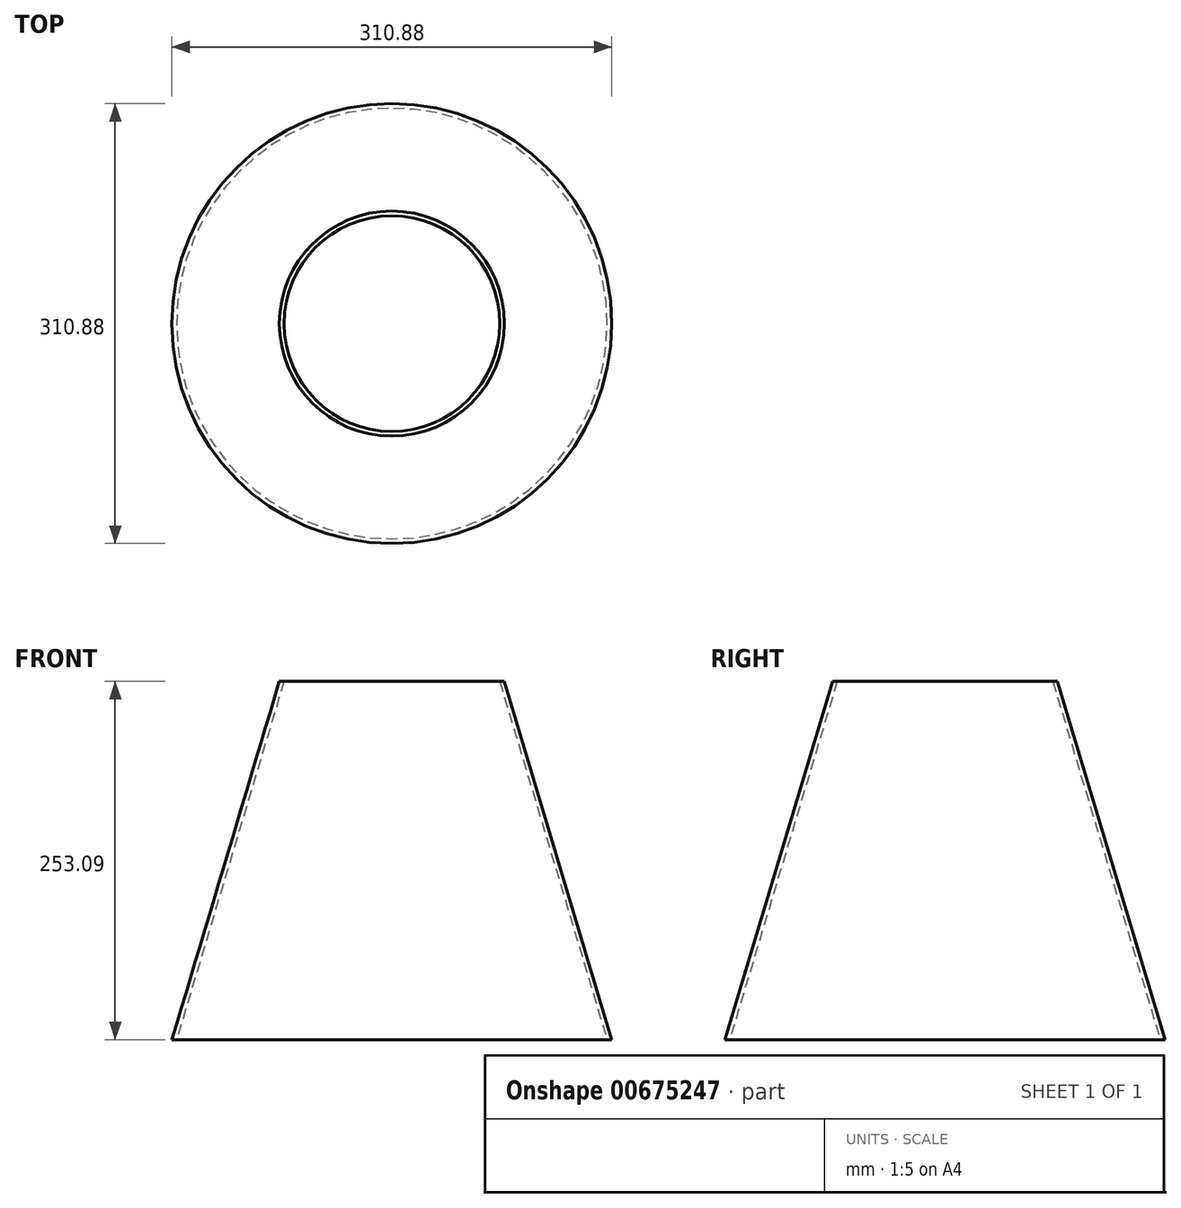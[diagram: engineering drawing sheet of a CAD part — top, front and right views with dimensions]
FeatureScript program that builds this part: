
annotation { "Feature Type Name" : "Feature", "Feature Type Description" : "" }
export const myFeature = defineFeature(function(context is Context, id is Id, definition is map)
    precondition{}
    {
        {
            var Q0;
            Q0=qCreatedBy(makeId("Front.planeOp"),FACE);
            var sketch = newSketch(context, id + "F0", { "sketchPlane" : qUnion([Q0])});
            skLineSegment(sketch, "E0", {"start": v(0, 0) * mm, "end": v(152.4, 0) * mm, "construction": true});
            skLineSegment(sketch, "E1", {"start": v(0, 0) * mm, "end": v(0, 254) * mm, "construction": true});
            skLineSegment(sketch, "E2", {"start": v(0, 254) * mm, "end": v(76.2, 254) * mm, "construction": true});
            skLineSegment(sketch, "E3", {"start": v(152.4, 0) * mm, "end": v(76.2, 254) * mm, "construction": true});
            skLineSegment(sketch, "E4.0", {"start": v(155.44, 0.91) * mm, "end": v(79.51, 254) * mm});
            skLineSegment(sketch, "E5", {"start": v(76.2, 254) * mm, "end": v(79.51, 254) * mm});
            skLineSegment(sketch, "E6", {"start": v(155.44, 0.91) * mm, "end": v(152.13, 0.91) * mm});
            skLineSegment(sketch, "E7", {"start": v(76.2, 254) * mm, "end": v(152.13, 0.91) * mm});
            skSolve(sketch);
        }
        {
            var Q0;
            Q0=makeQuery(id+"F0.imprint","IMPRINT",FACE,{"disambiguationData":[TD([[makeQuery(id+"F0.imprint","IMPRINT",EDGE,{"derivedFrom":sQuery(id+"F0.wireOp",EDGE,"E4.0")}),1.0]])]});
            var Q1;
            Q1=sQuery(id+"F0.wireOp",EDGE,"E1");
            revolve(context, id + "F1", {"entities" : qUnion([Q0]), "axis" : qUnion([Q1]), "revolveType" : RevolveType.FULL});
        }
    });
